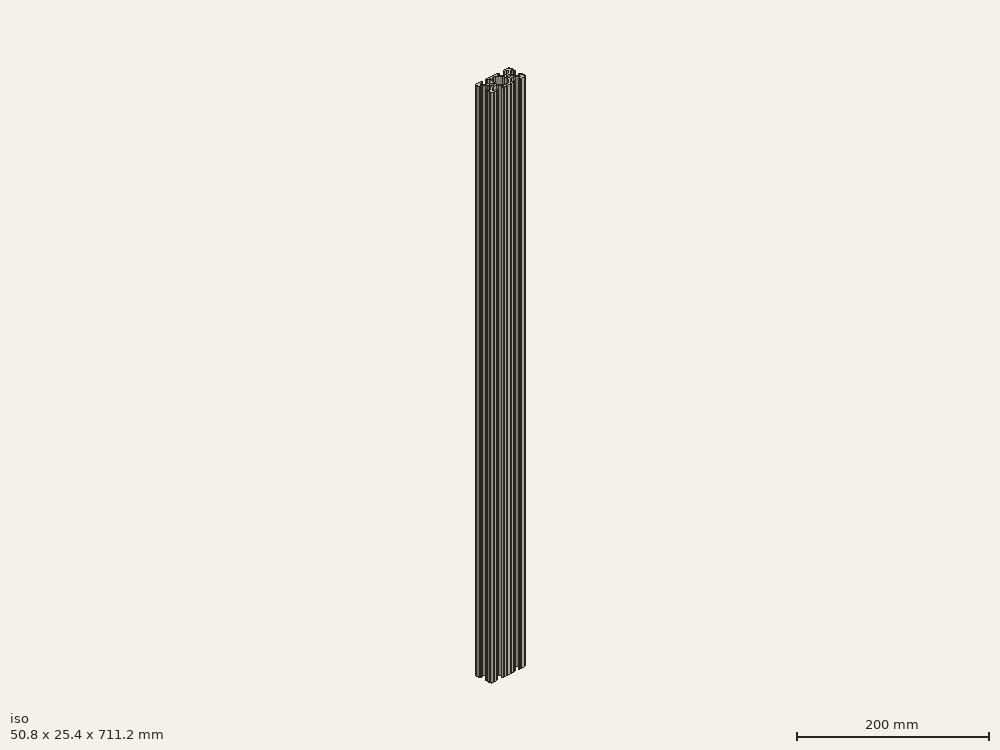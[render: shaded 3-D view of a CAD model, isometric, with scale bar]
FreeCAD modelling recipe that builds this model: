
FCSTD DOCUMENT  (FreeCAD 0.19R23756 (Git))
Label: 1020-28
License: All rights reserved
LicenseURL: http://en.wikipedia.org/wiki/All_rights_reserved
objects: Sketcher::SketchObject×1, Part::Extrusion×1
note: 2 computed .brp shape members not serialized (recipe doc carries the construction recipe); baked Part::Feature solids carry a one-line shape summary decoded from their .brp

FEATURE [Sketcher::SketchObject] Sketch162
  FullyConstrained = false
  sketch-geometry (162):
    g0: LineSegment StartX=7.25951 StartY=3.86941 StartZ=0 EndX=1.54575 EndY=9.57277 EndZ=0
    g1: LineSegment StartX=8.41248 StartY=-10.4902 StartZ=0 EndX=6.28364 EndY=-10.4902 EndZ=0
    g2: ArcOfCircle CenterX=8.41255 CenterY=-11.651 CenterZ=0 NormalX=0 NormalY=0 NormalZ=1 AngleXU=0 Radius=1.04895 StartAngle=4.71239 EndAngle=6.28319
    g3: LineSegment StartX=5.53258 StartY=-8.66607 StartZ=0 EndX=8.80999 EndY=-5.41626 EndZ=0
    g4: LineSegment StartX=9.4615 StartY=-11.651 StartZ=0 EndX=9.4615 EndY=-11.5392 EndZ=0
    g5: ArcOfCircle CenterX=8.41248 CenterY=-11.5392 CenterZ=0 NormalX=0 NormalY=0 NormalZ=1 AngleXU=0 Radius=1.04902 StartAngle=1.15714e-07 EndAngle=1.5708
    g6: ArcOfCircle CenterX=6.28364 CenterY=-9.42351 CenterZ=0 NormalX=0 NormalY=0 NormalZ=1 AngleXU=0 Radius=1.06669 StartAngle=2.35197 EndAngle=4.71239
    g7: LineSegment StartX=-7.28286 StartY=-3.84586 StartZ=0 EndX=-1.67557 EndY=-9.56109 EndZ=0
    g8: LineSegment StartX=1.50403 StartY=-9.57645 StartZ=0 EndX=7.25205 EndY=-3.87684 EndZ=0
    g9: LineSegment StartX=-0.551457 StartY=-10.033 StartZ=0 EndX=0.3952 EndY=-10.033 EndZ=0
    g10: LineSegment StartX=-1.54575 StartY=9.57277 StartZ=0 EndX=-7.25951 EndY=3.86941 EndZ=0
    g11: ArcOfCircle CenterX=0.3952 CenterY=-8.4582 CenterZ=0 NormalX=0 NormalY=0 NormalZ=1 AngleXU=0 Radius=1.5748 StartAngle=4.71239 EndAngle=5.49356
    g12: ArcOfCircle CenterX=5.0165 CenterY=-1.6223 CenterZ=0 NormalX=0 NormalY=0 NormalZ=1 AngleXU=0 Radius=3.175 StartAngle=5.49356 EndAngle=6.28319
    g13: LineSegment StartX=8.1915 StartY=-1.6223 StartZ=0 EndX=8.1915 EndY=1.6223 EndZ=0
    g14: LineSegment StartX=0.433213 StartY=10.033 StartZ=0 EndX=-0.433213 EndY=10.033 EndZ=0
    g15: ArcOfCircle CenterX=-0.551456 CenterY=-8.4582 CenterZ=0 NormalX=0 NormalY=0 NormalZ=1 AngleXU=0 Radius=1.5748 StartAngle=3.91746 EndAngle=4.71239
    g16: ArcOfCircle CenterX=-5.0165 CenterY=1.6223 CenterZ=0 NormalX=0 NormalY=0 NormalZ=1 AngleXU=0 Radius=3.175 StartAngle=2.35528 EndAngle=3.14159
    g17: ArcOfCircle CenterX=-0.433213 CenterY=8.4582 CenterZ=0 NormalX=0 NormalY=0 NormalZ=1 AngleXU=0 Radius=1.5748 StartAngle=1.5708 EndAngle=2.35528
    g18: ArcOfCircle CenterX=5.0165 CenterY=1.6223 CenterZ=0 NormalX=0 NormalY=0 NormalZ=1 AngleXU=0 Radius=3.175 StartAngle=2.15656e-07 EndAngle=0.78631
    g19: Circle CenterX=12.7 CenterY=-2.5e-15 CenterZ=0 NormalX=0 NormalY=0 NormalZ=-1 AngleXU=0 Radius=2.6035
    g20: Circle CenterX=-12.7 CenterY=2.5e-15 CenterZ=0 NormalX=0 NormalY=0 NormalZ=-1 AngleXU=0 Radius=2.6035
    g21: LineSegment StartX=-8.1915 StartY=1.6223 StartZ=0 EndX=-8.1915 EndY=-1.6223 EndZ=0
    g22: LineSegment StartX=-2.13358 StartY=-12.7 StartZ=0 EndX=2.13358 EndY=-12.7 EndZ=0
    g23: ArcOfCircle CenterX=-5.0165 CenterY=-1.6223 CenterZ=0 NormalX=0 NormalY=0 NormalZ=1 AngleXU=0 Radius=3.175 StartAngle=3.14159 EndAngle=3.91746
    g24: LineSegment StartX=3.14958 StartY=-12.7 StartZ=0 EndX=6.3669 EndY=-12.7 EndZ=0
    g25: ArcOfCircle CenterX=6.8749 CenterY=-12.7 CenterZ=0 NormalX=0 NormalY=0 NormalZ=1 AngleXU=0 Radius=0.508 StartAngle=0 EndAngle=3.14159
    g26: LineSegment StartX=-6.28939 StartY=-10.4902 StartZ=0 EndX=-8.41248 EndY=-10.4902 EndZ=0
    g27: LineSegment StartX=-8.41255 StartY=-12.7 StartZ=0 EndX=-7.38288 EndY=-12.7 EndZ=0
    g28: ArcOfCircle CenterX=0.433213 CenterY=8.4582 CenterZ=0 NormalX=0 NormalY=0 NormalZ=1 AngleXU=0 Radius=1.5748 StartAngle=0.78631 EndAngle=1.5708
    g29: ArcOfCircle CenterX=2.64158 CenterY=-12.7 CenterZ=0 NormalX=0 NormalY=0 NormalZ=1 AngleXU=0 Radius=0.508 StartAngle=0 EndAngle=3.14159
    g30: ArcOfCircle CenterX=-16.9875 CenterY=-11.5392 CenterZ=0 NormalX=0 NormalY=0 NormalZ=1 AngleXU=0 Radius=1.04902 StartAngle=1.16223e-07 EndAngle=1.5708
    g31: LineSegment StartX=-8.81696 StartY=-5.44724 StartZ=0 EndX=-5.56415 EndY=-8.76265 EndZ=0
    g32: LineSegment StartX=-16.9875 StartY=-10.4902 StartZ=0 EndX=-19.1164 EndY=-10.4902 EndZ=0
    g33: ArcOfCircle CenterX=-11.0833 CenterY=-7.6708 CenterZ=0 NormalX=0 NormalY=0 NormalZ=1 AngleXU=0 Radius=3.175 StartAngle=0.775866 EndAngle=1.5708
    g34: ArcOfCircle CenterX=-14.3449 CenterY=-7.6708 CenterZ=0 NormalX=0 NormalY=0 NormalZ=1 AngleXU=0 Radius=3.175 StartAngle=1.5708 EndAngle=2.3692
    g35: ArcOfCircle CenterX=-19.1164 CenterY=-9.4742 CenterZ=0 NormalX=0 NormalY=0 NormalZ=1 AngleXU=0 Radius=1.016 StartAngle=2.3692 EndAngle=4.71239
    g36: ArcOfCircle CenterX=-8.41248 CenterY=-11.5392 CenterZ=0 NormalX=0 NormalY=0 NormalZ=1 AngleXU=0 Radius=1.04902 StartAngle=1.5708 EndAngle=3.14159
    g37: LineSegment StartX=7.3829 StartY=-12.7 StartZ=0 EndX=8.41255 EndY=-12.7 EndZ=0
    g38: ArcOfCircle CenterX=-8.41255 CenterY=-11.651 CenterZ=0 NormalX=0 NormalY=0 NormalZ=1 AngleXU=0 Radius=1.04895 StartAngle=3.14159 EndAngle=4.71239
    g39: ArcOfCircle CenterX=14.3545 CenterY=-7.6708 CenterZ=0 NormalX=0 NormalY=0 NormalZ=1 AngleXU=0 Radius=3.175 StartAngle=0.789627 EndAngle=1.5708
    g40: ArcOfCircle CenterX=20.3835 CenterY=-1.55362 CenterZ=0 NormalX=0 NormalY=0 NormalZ=1 AngleXU=0 Radius=3.175 StartAngle=3.14159 EndAngle=3.93122
    g41: LineSegment StartX=23.1902 StartY=6.498 StartZ=0 EndX=23.1902 EndY=4.28752 EndZ=0
    g42: LineSegment StartX=-14.3449 StartY=-4.4958 StartZ=0 EndX=-11.0833 EndY=-4.4958 EndZ=0
    g43: LineSegment StartX=-19.8441 StartY=-8.76517 StartZ=0 EndX=-16.619 EndY=-5.45511 EndZ=0
    g44: LineSegment StartX=-6.36688 StartY=-12.7 StartZ=0 EndX=-3.14958 EndY=-12.7 EndZ=0
    g45: ArcOfCircle CenterX=-6.28939 CenterY=-9.4742 CenterZ=0 NormalX=0 NormalY=0 NormalZ=1 AngleXU=0 Radius=1.016 StartAngle=4.71239 EndAngle=7.05905
    g46: LineSegment StartX=-9.4615 StartY=-11.5392 StartZ=0 EndX=-9.4615 EndY=-11.6511 EndZ=0
    g47: ArcOfCircle CenterX=-6.87488 CenterY=-12.7 CenterZ=0 NormalX=0 NormalY=0 NormalZ=1 AngleXU=0 Radius=0.508 StartAngle=0 EndAngle=3.14159
    g48: LineSegment StartX=-15.9385 StartY=-11.651 StartZ=0 EndX=-15.9385 EndY=-11.5392 EndZ=0
    g49: ArcOfCircle CenterX=-2.64158 CenterY=-12.7 CenterZ=0 NormalX=0 NormalY=0 NormalZ=1 AngleXU=0 Radius=0.508 StartAngle=0 EndAngle=3.14159
    g50: ArcOfCircle CenterX=22.1596 CenterY=-6.33474 CenterZ=0 NormalX=0 NormalY=0 NormalZ=1 AngleXU=0 Radius=1.03057 StartAngle=3.93122 EndAngle=6.28319
    g51: ArcOfCircle CenterX=25.4 CenterY=5.82513 CenterZ=0 NormalX=0 NormalY=0 NormalZ=1 AngleXU=0 Radius=0.508 StartAngle=1.5708 EndAngle=4.71239
    g52: LineSegment StartX=25.4 StartY=6.33313 StartZ=0 EndX=25.4 EndY=9.5504 EndZ=0
    g53: LineSegment StartX=19.0331 StartY=-12.7 StartZ=0 EndX=22.2504 EndY=-12.7 EndZ=0
    g54: ArcOfCircle CenterX=20.3835 CenterY=1.69518 CenterZ=0 NormalX=0 NormalY=0 NormalZ=1 AngleXU=0 Radius=3.175 StartAngle=2.35528 EndAngle=3.14159
    g55: LineSegment StartX=16.9875 StartY=-12.7 StartZ=0 EndX=18.0171 EndY=-12.7 EndZ=0
    g56: ArcOfCircle CenterX=23.2918 CenterY=10.5918 CenterZ=0 NormalX=0 NormalY=0 NormalZ=1 AngleXU=0 Radius=2.1082 StartAngle=6.27114 EndAngle=7.86603
    g57: ArcOfCircle CenterX=24.2392 CenterY=-4.28752 CenterZ=0 NormalX=0 NormalY=0 NormalZ=1 AngleXU=0 Radius=1.04902 StartAngle=1.5708 EndAngle=3.14159
    g58: ArcOfCircle CenterX=24.401 CenterY=-4.23752 CenterZ=0 NormalX=0 NormalY=0 NormalZ=1 AngleXU=0 Radius=0.99902 StartAngle=1.41033e-07 EndAngle=1.5708
    g59: LineSegment StartX=16.59 StartY=-5.41626 StartZ=0 EndX=19.8674 EndY=-8.66607 EndZ=0
    g60: ArcOfCircle CenterX=16.9875 CenterY=-11.5392 CenterZ=0 NormalX=0 NormalY=0 NormalZ=1 AngleXU=0 Radius=1.04902 StartAngle=1.5708 EndAngle=3.14159
    g61: LineSegment StartX=22.2504 StartY=12.7 StartZ=0 EndX=19.0331 EndY=12.7 EndZ=0
    g62: ArcOfCircle CenterX=23.2918 CenterY=-10.5918 CenterZ=0 NormalX=0 NormalY=0 NormalZ=1 AngleXU=0 Radius=2.1082 StartAngle=4.70034 EndAngle=6.29523
    g63: ArcOfCircle CenterX=11.0455 CenterY=-7.6708 CenterZ=0 NormalX=0 NormalY=0 NormalZ=1 AngleXU=0 Radius=3.175 StartAngle=1.5708 EndAngle=2.35197
    g64: ArcOfCircle CenterX=22.7584 CenterY=12.7 CenterZ=0 NormalX=0 NormalY=0 NormalZ=1 AngleXU=0 Radius=0.508 StartAngle=3.14159 EndAngle=6.28288
    g65: LineSegment StartX=19.1164 StartY=-10.4902 StartZ=0 EndX=16.9875 EndY=-10.4902 EndZ=0
    g66: ArcOfCircle CenterX=22.7584 CenterY=-12.7 CenterZ=0 NormalX=0 NormalY=0 NormalZ=1 AngleXU=0 Radius=0.508 StartAngle=0.000301216 EndAngle=3.14159
    g67: ArcOfCircle CenterX=16.9875 CenterY=11.651 CenterZ=0 NormalX=0 NormalY=0 NormalZ=1 AngleXU=0 Radius=1.04902 StartAngle=1.5708 EndAngle=3.14159
    g68: ArcOfCircle CenterX=24.351 CenterY=4.28752 CenterZ=0 NormalX=0 NormalY=0 NormalZ=1 AngleXU=0 Radius=1.04902 StartAngle=4.71239 EndAngle=6.28319
    g69: ArcOfCircle CenterX=19.1164 CenterY=9.4742 CenterZ=0 NormalX=0 NormalY=0 NormalZ=1 AngleXU=0 Radius=1.016 StartAngle=5.49688 EndAngle=7.85398
    g70: LineSegment StartX=19.8341 StartY=8.75512 StartZ=0 EndX=16.4966 EndY=5.42369 EndZ=0
    g71: LineSegment StartX=18.0171 StartY=12.7 StartZ=0 EndX=16.9875 EndY=12.7 EndZ=0
    g72: ArcOfCircle CenterX=18.5251 CenterY=-12.7 CenterZ=0 NormalX=0 NormalY=0 NormalZ=1 AngleXU=0 Radius=0.508 StartAngle=0 EndAngle=3.14159
    g73: LineSegment StartX=15.9384 StartY=11.651 StartZ=0 EndX=15.9384 EndY=11.5392 EndZ=0
    g74: LineSegment StartX=16.9875 StartY=10.4902 StartZ=0 EndX=19.1164 EndY=10.4902 EndZ=0
    g75: LineSegment StartX=11.0455 StartY=-4.4958 StartZ=0 EndX=14.3545 EndY=-4.4958 EndZ=0
    g76: ArcOfCircle CenterX=14.2536 CenterY=7.6708 CenterZ=0 NormalX=0 NormalY=0 NormalZ=1 AngleXU=0 Radius=3.175 StartAngle=4.71239 EndAngle=5.49688
    g77: ArcOfCircle CenterX=25.4 CenterY=-5.82508 CenterZ=0 NormalX=0 NormalY=0 NormalZ=1 AngleXU=0 Radius=0.508 StartAngle=1.5708 EndAngle=4.71239
    g78: LineSegment StartX=18.1405 StartY=3.94229 StartZ=0 EndX=21.4316 EndY=7.22739 EndZ=0
    g79: LineSegment StartX=25.4 StartY=-5.31708 StartZ=0 EndX=25.4 EndY=-4.23752 EndZ=0
    g80: LineSegment StartX=14.2536 StartY=4.4958 StartZ=0 EndX=11.1464 EndY=4.4958 EndZ=0
    g81: ArcOfCircle CenterX=18.5251 CenterY=12.7 CenterZ=0 NormalX=0 NormalY=0 NormalZ=1 AngleXU=0 Radius=0.508 StartAngle=3.14159 EndAngle=6.28319
    g82: LineSegment StartX=23.1902 StartY=-4.28752 StartZ=0 EndX=23.1902 EndY=-6.33474 EndZ=0
    g83: LineSegment StartX=24.401 StartY=-3.2385 StartZ=0 EndX=24.2392 EndY=-3.2385 EndZ=0
    g84: ArcOfCircle CenterX=22.1596 CenterY=6.498 CenterZ=0 NormalX=0 NormalY=0 NormalZ=1 AngleXU=0 Radius=1.03057 StartAngle=0 EndAngle=2.35528
    g85: LineSegment StartX=15.9385 StartY=-11.5392 StartZ=0 EndX=15.9385 EndY=-11.6511 EndZ=0
    g86: LineSegment StartX=25.4 StartY=4.28752 StartZ=0 EndX=25.4 EndY=5.31713 EndZ=0
    g87: ArcOfCircle CenterX=11.1464 CenterY=7.6708 CenterZ=0 NormalX=0 NormalY=0 NormalZ=1 AngleXU=0 Radius=3.175 StartAngle=3.9279 EndAngle=4.71239
    g88: LineSegment StartX=8.90339 StartY=5.42369 StartZ=0 EndX=5.56588 EndY=8.75512 EndZ=0
    g89: LineSegment StartX=21.434 StartY=-7.06654 StartZ=0 EndX=18.148 EndY=-3.80816 EndZ=0
    g90: ArcOfCircle CenterX=25.4 CenterY=10.0584 CenterZ=0 NormalX=0 NormalY=0 NormalZ=1 AngleXU=0 Radius=0.508 StartAngle=1.5711 EndAngle=4.71239
    g91: ArcOfCircle CenterX=16.9875 CenterY=-11.651 CenterZ=0 NormalX=0 NormalY=0 NormalZ=1 AngleXU=0 Radius=1.04895 StartAngle=3.14159 EndAngle=4.71239
    g92: ArcOfCircle CenterX=19.1164 CenterY=-9.42352 CenterZ=0 NormalX=0 NormalY=0 NormalZ=1 AngleXU=0 Radius=1.06668 StartAngle=4.71239 EndAngle=7.07281
    g93: ArcOfCircle CenterX=24.2392 CenterY=4.28752 CenterZ=0 NormalX=0 NormalY=0 NormalZ=1 AngleXU=0 Radius=1.04902 StartAngle=3.14159 EndAngle=4.71239
    g94: ArcOfCircle CenterX=16.9875 CenterY=11.5392 CenterZ=0 NormalX=0 NormalY=0 NormalZ=1 AngleXU=0 Radius=1.04902 StartAngle=3.14159 EndAngle=4.71239
    g95: ArcOfCircle CenterX=25.4 CenterY=-10.0584 CenterZ=0 NormalX=0 NormalY=0 NormalZ=1 AngleXU=0 Radius=0.508 StartAngle=1.5708 EndAngle=4.71209
    g96: ArcOfCircle CenterX=6.87487 CenterY=12.7 CenterZ=0 NormalX=0 NormalY=0 NormalZ=1 AngleXU=0 Radius=0.508 StartAngle=3.14159 EndAngle=6.28319
    g97: LineSegment StartX=25.4 StartY=-9.5504 StartZ=0 EndX=25.4 EndY=-6.33308 EndZ=0
    g98: LineSegment StartX=17.2085 StartY=-1.55362 StartZ=0 EndX=17.2085 EndY=1.69518 EndZ=0
    g99: LineSegment StartX=-9.46155 StartY=11.651 StartZ=0 EndX=-9.46155 EndY=11.5392 EndZ=0
    g100: LineSegment StartX=24.2392 StartY=3.2385 StartZ=0 EndX=24.351 EndY=3.2385 EndZ=0
    g101: LineSegment StartX=-8.41253 StartY=10.4902 StartZ=0 EndX=-6.28939 EndY=10.4902 EndZ=0
    g102: ArcOfCircle CenterX=-10.8409 CenterY=7.6708 CenterZ=0 NormalX=0 NormalY=0 NormalZ=1 AngleXU=0 Radius=3.175 StartAngle=4.71239 EndAngle=5.49688
    g103: LineSegment StartX=-19.1164 StartY=10.4902 StartZ=0 EndX=-16.9875 EndY=10.4902 EndZ=0
    g104: LineSegment StartX=-10.8409 StartY=4.4958 StartZ=0 EndX=-14.1026 EndY=4.4958 EndZ=0
    g105: LineSegment StartX=-16.1879 StartY=5.27664 StartZ=0 EndX=-19.8682 EndY=8.48225 EndZ=0
    g106: LineSegment StartX=-7.38291 StartY=12.7 StartZ=0 EndX=-8.41253 EndY=12.7 EndZ=0
    g107: ArcOfCircle CenterX=-6.28939 CenterY=9.34546 CenterZ=0 NormalX=0 NormalY=0 NormalZ=1 AngleXU=0 Radius=1.14474 StartAngle=5.49688 EndAngle=7.85398
    g108: LineSegment StartX=6.28364 StartY=10.4902 StartZ=0 EndX=8.41253 EndY=10.4902 EndZ=0
    g109: ArcOfCircle CenterX=8.41253 CenterY=11.651 CenterZ=0 NormalX=0 NormalY=0 NormalZ=1 AngleXU=0 Radius=1.04902 StartAngle=4.29175e-07 EndAngle=1.5708
    g110: LineSegment StartX=9.46155 StartY=11.5392 StartZ=0 EndX=9.46155 EndY=11.651 EndZ=0
    g111: ArcOfCircle CenterX=-14.1026 CenterY=7.6708 CenterZ=0 NormalX=0 NormalY=0 NormalZ=1 AngleXU=0 Radius=3.175 StartAngle=3.99583 EndAngle=4.71239
    g112: LineSegment StartX=-5.48068 StartY=8.53527 StartZ=0 EndX=-8.59793 EndY=5.42369 EndZ=0
    g113: ArcOfCircle CenterX=-19.1164 CenterY=9.34546 CenterZ=0 NormalX=0 NormalY=0 NormalZ=1 AngleXU=0 Radius=1.14474 StartAngle=1.5708 EndAngle=3.99583
    g114: LineSegment StartX=8.41253 StartY=12.7 StartZ=0 EndX=7.38287 EndY=12.7 EndZ=0
    g115: LineSegment StartX=-3.14958 StartY=12.7 StartZ=0 EndX=-6.36691 EndY=12.7 EndZ=0
    g116: ArcOfCircle CenterX=-8.41253 CenterY=11.5392 CenterZ=0 NormalX=0 NormalY=0 NormalZ=1 AngleXU=0 Radius=1.04902 StartAngle=3.14159 EndAngle=4.71239
    g117: ArcOfCircle CenterX=8.41253 CenterY=11.5392 CenterZ=0 NormalX=0 NormalY=0 NormalZ=1 AngleXU=0 Radius=1.04902 StartAngle=4.71239 EndAngle=6.28319
    g118: ArcOfCircle CenterX=-6.87491 CenterY=12.7 CenterZ=0 NormalX=0 NormalY=0 NormalZ=1 AngleXU=0 Radius=0.508 StartAngle=3.14159 EndAngle=6.28319
    g119: ArcOfCircle CenterX=-8.41253 CenterY=11.651 CenterZ=0 NormalX=0 NormalY=0 NormalZ=1 AngleXU=0 Radius=1.04902 StartAngle=1.5708 EndAngle=3.14159
    g120: ArcOfCircle CenterX=-2.64159 CenterY=12.7 CenterZ=0 NormalX=0 NormalY=0 NormalZ=1 AngleXU=0 Radius=0.507987 StartAngle=3.14159 EndAngle=6.28319
    g121: ArcOfCircle CenterX=6.28364 CenterY=9.4742 CenterZ=0 NormalX=0 NormalY=0 NormalZ=1 AngleXU=0 Radius=1.016 StartAngle=1.5708 EndAngle=3.9279
    g122: LineSegment StartX=2.13361 StartY=12.7 StartZ=0 EndX=-2.13361 EndY=12.7 EndZ=0
    g123: LineSegment StartX=6.36687 StartY=12.7 StartZ=0 EndX=3.14961 EndY=12.7 EndZ=0
    g124: ArcOfCircle CenterX=-24.401 CenterY=4.23752 CenterZ=0 NormalX=0 NormalY=0 NormalZ=1 AngleXU=0 Radius=0.99902 StartAngle=3.14159 EndAngle=4.71239
    g125: LineSegment StartX=-16.9875 StartY=12.7 StartZ=0 EndX=-18.0171 EndY=12.7 EndZ=0
    g126: LineSegment StartX=-24.401 StartY=3.2385 StartZ=0 EndX=-24.1892 EndY=3.2385 EndZ=0
    g127: ArcOfCircle CenterX=2.64161 CenterY=12.7 CenterZ=0 NormalX=0 NormalY=0 NormalZ=1 AngleXU=0 Radius=0.508 StartAngle=3.14159 EndAngle=6.28319
    g128: ArcOfCircle CenterX=-22.2207 CenterY=-6.67687 CenterZ=0 NormalX=0 NormalY=0 NormalZ=1 AngleXU=0 Radius=0.969476 StartAngle=3.14159 EndAngle=5.51079
    g129: LineSegment StartX=-18.1094 StartY=-3.8465 StartZ=0 EndX=-21.5263 EndY=-7.35342 EndZ=0
    g130: LineSegment StartX=-17.2085 StartY=1.63081 StartZ=0 EndX=-17.2085 EndY=-1.63081 EndZ=0
    g131: ArcOfCircle CenterX=-22.2207 CenterY=6.15588 CenterZ=0 NormalX=0 NormalY=0 NormalZ=1 AngleXU=0 Radius=0.969476 StartAngle=0.854233 EndAngle=3.14159
    g132: LineSegment StartX=-24.1892 StartY=-3.2385 StartZ=0 EndX=-24.401 EndY=-3.2385 EndZ=0
    g133: ArcOfCircle CenterX=-25.4 CenterY=10.0584 CenterZ=0 NormalX=0 NormalY=0 NormalZ=1 AngleXU=0 Radius=0.508 StartAngle=4.71239 EndAngle=7.85368
    g134: LineSegment StartX=-23.1902 StartY=-6.67687 StartZ=0 EndX=-23.1902 EndY=-4.23752 EndZ=0
    g135: ArcOfCircle CenterX=-20.3835 CenterY=-1.63081 CenterZ=0 NormalX=0 NormalY=0 NormalZ=1 AngleXU=0 Radius=3.175 StartAngle=5.51079 EndAngle=6.28319
    g136: ArcOfCircle CenterX=-24.1892 CenterY=-4.23752 CenterZ=0 NormalX=0 NormalY=0 NormalZ=1 AngleXU=0 Radius=0.99902 StartAngle=1.41033e-07 EndAngle=1.5708
    g137: ArcOfCircle CenterX=-25.4 CenterY=5.82508 CenterZ=0 NormalX=0 NormalY=0 NormalZ=1 AngleXU=0 Radius=0.508 StartAngle=4.71239 EndAngle=7.85398
    g138: LineSegment StartX=-23.1902 StartY=4.23752 StartZ=0 EndX=-23.1902 EndY=6.15588 EndZ=0
    g139: LineSegment StartX=-15.9384 StartY=11.5392 StartZ=0 EndX=-15.9384 EndY=11.651 EndZ=0
    g140: ArcOfCircle CenterX=-22.7584 CenterY=12.7 CenterZ=0 NormalX=0 NormalY=0 NormalZ=1 AngleXU=0 Radius=0.508 StartAngle=3.14189 EndAngle=6.28319
    g141: LineSegment StartX=-19.0331 StartY=12.7 StartZ=0 EndX=-22.2504 EndY=12.7 EndZ=0
    g142: ArcOfCircle CenterX=-16.9875 CenterY=11.651 CenterZ=0 NormalX=0 NormalY=0 NormalZ=1 AngleXU=0 Radius=1.04902 StartAngle=4.28571e-07 EndAngle=1.5708
    g143: ArcOfCircle CenterX=-18.5251 CenterY=12.7 CenterZ=0 NormalX=0 NormalY=0 NormalZ=1 AngleXU=0 Radius=0.508 StartAngle=3.14159 EndAngle=6.28319
    g144: ArcOfCircle CenterX=-24.1892 CenterY=4.23752 CenterZ=0 NormalX=0 NormalY=0 NormalZ=1 AngleXU=0 Radius=0.99902 StartAngle=4.71239 EndAngle=6.28319
    g145: LineSegment StartX=-25.4 StartY=5.31708 StartZ=0 EndX=-25.4 EndY=4.23752 EndZ=0
    g146: ArcOfCircle CenterX=-16.9875 CenterY=11.5392 CenterZ=0 NormalX=0 NormalY=0 NormalZ=1 AngleXU=0 Radius=1.04902 StartAngle=4.71239 EndAngle=6.28319
    g147: LineSegment StartX=-21.584 StartY=6.88693 StartZ=0 EndX=-18.2982 EndY=4.02497 EndZ=0
    g148: ArcOfCircle CenterX=-20.3835 CenterY=1.63081 CenterZ=0 NormalX=0 NormalY=0 NormalZ=1 AngleXU=0 Radius=3.175 StartAngle=0 EndAngle=0.854233
    g149: ArcOfCircle CenterX=-23.2918 CenterY=10.5918 CenterZ=0 NormalX=0 NormalY=0 NormalZ=1 AngleXU=0 Radius=2.1082 StartAngle=1.55875 EndAngle=3.15364
    g150: LineSegment StartX=-25.4 StartY=9.5504 StartZ=0 EndX=-25.4 EndY=6.33308 EndZ=0
    g151: LineSegment StartX=-25.4 StartY=-4.23752 StartZ=0 EndX=-25.4 EndY=-5.31708 EndZ=0
    g152: ArcOfCircle CenterX=-23.2918 CenterY=-10.5918 CenterZ=0 NormalX=0 NormalY=0 NormalZ=1 AngleXU=0 Radius=2.1082 StartAngle=3.12954 EndAngle=4.72444
    g153: ArcOfCircle CenterX=-22.7584 CenterY=-12.7 CenterZ=0 NormalX=0 NormalY=0 NormalZ=1 AngleXU=0 Radius=0.508 StartAngle=0 EndAngle=3.14129
    g154: LineSegment StartX=-18.0171 StartY=-12.7 StartZ=0 EndX=-16.9875 EndY=-12.7 EndZ=0
    g155: ArcOfCircle CenterX=-25.4 CenterY=-10.0584 CenterZ=0 NormalX=0 NormalY=0 NormalZ=1 AngleXU=0 Radius=0.508 StartAngle=4.71269 EndAngle=7.85398
    g156: LineSegment StartX=-22.2504 StartY=-12.7 StartZ=0 EndX=-19.0331 EndY=-12.7 EndZ=0
    g157: ArcOfCircle CenterX=-16.9875 CenterY=-11.651 CenterZ=0 NormalX=0 NormalY=0 NormalZ=1 AngleXU=0 Radius=1.04895 StartAngle=4.71239 EndAngle=6.28319
    g158: ArcOfCircle CenterX=-24.401 CenterY=-4.23752 CenterZ=0 NormalX=0 NormalY=0 NormalZ=1 AngleXU=0 Radius=0.99902 StartAngle=1.5708 EndAngle=3.14159
    g159: ArcOfCircle CenterX=-25.4 CenterY=-5.82513 CenterZ=0 NormalX=0 NormalY=0 NormalZ=1 AngleXU=0 Radius=0.508051 StartAngle=4.71239 EndAngle=7.85398
    g160: ArcOfCircle CenterX=-18.5251 CenterY=-12.7 CenterZ=0 NormalX=0 NormalY=0 NormalZ=1 AngleXU=0 Radius=0.508 StartAngle=0 EndAngle=3.14159
    g161: LineSegment StartX=-25.4 StartY=-6.33319 StartZ=0 EndX=-25.4 EndY=-9.5504 EndZ=0
  constraints (160):
    c: Coincident(g161,g155)
    c: Coincident(g159,g161)
    c: Coincident(g151,g159)
    c: Coincident(g158,g151)
    c: Coincident(g124,g145)
    c: Coincident(g137,g145)
    c: Coincident(g137,g150)
    c: Coincident(g133,g150)
    c: Coincident(g152,g155)
    c: Coincident(g149,g133)
    c: Coincident(g158,g132)
    c: Coincident(g124,g126)
    c: Coincident(g136,g132)
    c: Coincident(g144,g126)
    c: Coincident(g153,g152)
    c: Coincident(g140,g149)
    c: Coincident(g134,g128)
    c: Coincident(g134,g136)
    c: Coincident(g138,g144)
    c: Coincident(g131,g138)
    c: Coincident(g153,g156)
    c: Coincident(g141,g140)
    c: Coincident(g131,g147)
    c: Coincident(g129,g128)
    c: Coincident(g105,g113)
    c: Coincident(g35,g43)
    c: Coincident(g35,g32)
    c: Coincident(g113,g103)
    c: Coincident(g156,g160)
    c: Coincident(g143,g141)
    c: Coincident(g147,g148)
    c: Coincident(g135,g129)
    c: Coincident(g154,g160)
    c: Coincident(g143,g125)
    c: Coincident(g130,g135)
    c: Coincident(g130,g148)
    c: Coincident(g154,g157)
    c: Coincident(g32,g30)
    c: Coincident(g103,g146)
    c: Coincident(g142,g125)
    c: Coincident(g43,g34)
    c: Coincident(g111,g105)
    c: Coincident(g157,g48)
    c: Coincident(g48,g30)
    c: Coincident(g139,g146)
    c: Coincident(g139,g142)
    c: Coincident(g42,g34)
    c: Coincident(g104,g111)
    c: Coincident(g33,g42)
    c: Coincident(g102,g104)
    c: Coincident(g38,g46)
    c: Coincident(g46,g36)
    c: Coincident(g99,g116)
    c: Coincident(g119,g99)
    c: Coincident(g33,g31)
    c: Coincident(g102,g112)
    c: Coincident(g27,g38)
    c: Coincident(g36,g26)
    c: Coincident(g116,g101)
    c: Coincident(g106,g119)
    c: Coincident(g21,g23)
    c: Coincident(g21,g16)
    c: Coincident(g27,g47)
    c: Coincident(g106,g118)
    c: Coincident(g23,g7)
    c: Coincident(g10,g16)
    c: Coincident(g44,g47)
    c: Coincident(g118,g115)
    c: Coincident(g45,g26)
    c: Coincident(g107,g101)
    c: Coincident(g45,g31)
    c: Coincident(g112,g107)
    c: Coincident(g44,g49)
    c: Coincident(g120,g115)
    c: Coincident(g22,g49)
    c: Coincident(g122,g120)
    c: Coincident(g15,g7)
    c: Coincident(g10,g17)
    c: Coincident(g9,g15)
    c: Coincident(g17,g14)
    c: Coincident(g9,g11)
    c: Coincident(g14,g28)
    c: Coincident(g8,g11)
    c: Coincident(g0,g28)
    c: Coincident(g29,g22)
    c: Coincident(g122,g127)
    c: Coincident(g24,g29)
    c: Coincident(g123,g127)
    c: Coincident(g3,g6)
    c: Coincident(g88,g121)
    c: Coincident(g1,g6)
    c: Coincident(g108,g121)
    c: Coincident(g25,g24)
    c: Coincident(g96,g123)
    c: Coincident(g8,g12)
    c: Coincident(g18,g0)
    c: Coincident(g25,g37)
    c: Coincident(g96,g114)
    c: Coincident(g12,g13)
    c: Coincident(g18,g13)
    c: Coincident(g2,g37)
    c: Coincident(g5,g1)
    c: Coincident(g117,g108)
    c: Coincident(g109,g114)
    c: Coincident(g3,g63)
    c: Coincident(g87,g88)
    c: Coincident(g2,g4)
    c: Coincident(g5,g4)
    c: Coincident(g117,g110)
    c: Coincident(g109,g110)
    c: Coincident(g75,g63)
    c: Coincident(g80,g87)
    c: Coincident(g80,g76)
    c: Coincident(g39,g75)
    c: Coincident(g85,g91)
    c: Coincident(g85,g60)
    c: Coincident(g73,g94)
    c: Coincident(g73,g67)
    c: Coincident(g70,g76)
    c: Coincident(g59,g39)
    c: Coincident(g55,g91)
    c: Coincident(g60,g65)
    c: Coincident(g94,g74)
    c: Coincident(g67,g71)
    c: Coincident(g40,g98)
    c: Coincident(g54,g98)
    c: Coincident(g55,g72)
    c: Coincident(g71,g81)
    c: Coincident(g78,g54)
    c: Coincident(g40,g89)
    c: Coincident(g53,g72)
    c: Coincident(g61,g81)
    c: Coincident(g65,g92)
    c: Coincident(g74,g69)
    c: Coincident(g70,g69)
    c: Coincident(g59,g92)
    c: Coincident(g84,g78)
    c: Coincident(g50,g89)
    c: Coincident(g53,g66)
    c: Coincident(g64,g61)
    c: Coincident(g82,g50)
    c: Coincident(g57,g82)
    c: Coincident(g41,g93)
    c: Coincident(g41,g84)
    c: Coincident(g62,g66)
    c: Coincident(g64,g56)
    c: Coincident(g57,g83)
    c: Coincident(g100,g93)
    c: Coincident(g100,g68)
    c: Coincident(g58,g83)
    c: Coincident(g62,g95)
    c: Coincident(g56,g90)
    c: Coincident(g97,g95)
    c: Coincident(g97,g77)
    c: Coincident(g77,g79)
    c: Coincident(g58,g79)
    c: Coincident(g68,g86)
    c: Coincident(g86,g51)
    c: Coincident(g51,g52)
    c: Coincident(g52,g90)
FEATURE [Part::Extrusion] Extrude
  Base = -> Sketch162
  Dir = (0,0,1)
  DirMode = 2
  FaceMakerClass = Part::FaceMakerBullseye
  LengthFwd = 711.2
  LengthRev = 0
  Solid = true
  Symmetric = false
